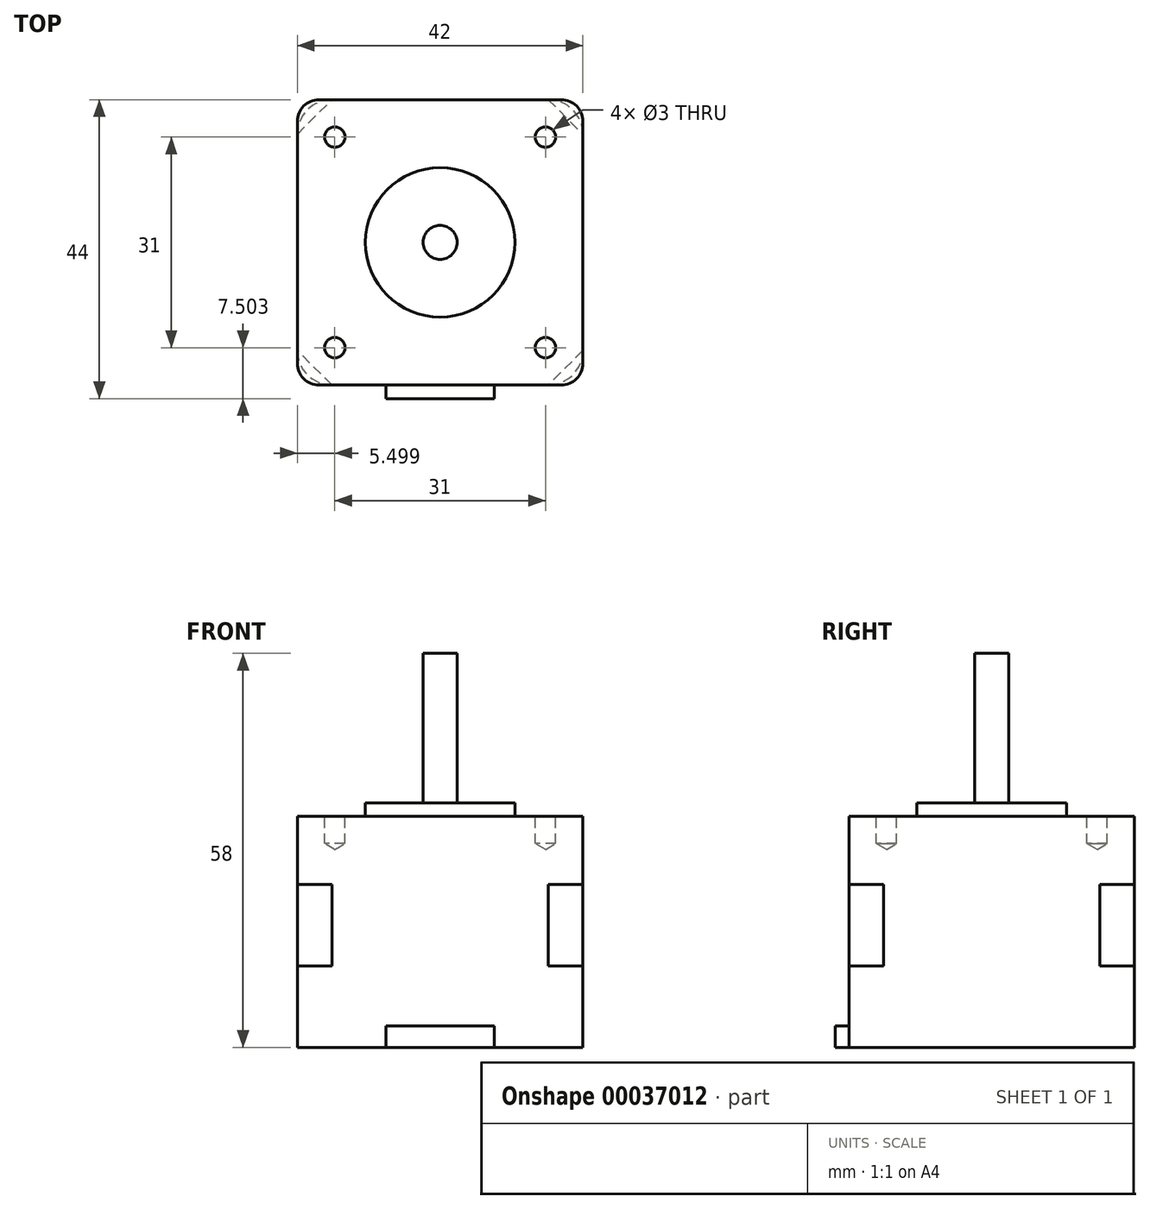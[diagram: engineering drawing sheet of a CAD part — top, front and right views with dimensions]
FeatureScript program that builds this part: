
annotation { "Feature Type Name" : "Feature", "Feature Type Description" : "" }
export const myFeature = defineFeature(function(context is Context, id is Id, definition is map)
    precondition{}
    {
        {
            var Q0;
            Q0=qCreatedBy(makeId("Top.planeOp"),FACE);
            var sketch = newSketch(context, id + "F0", { "sketchPlane" : qUnion([Q0])});
            skLineSegment(sketch, "E0.bottom", {"start": v(-20.04, 16.68) * mm, "end": v(21.96, 16.68) * mm});
            skLineSegment(sketch, "E0.top", {"start": v(-20.04, -25.32) * mm, "end": v(21.96, -25.32) * mm});
            skLineSegment(sketch, "E0.left", {"start": v(-20.04, 16.68) * mm, "end": v(-20.04, -25.32) * mm});
            skLineSegment(sketch, "E0.right", {"start": v(21.96, 16.68) * mm, "end": v(21.96, -25.32) * mm});
            skSolve(sketch);
        }
        {
            var Q0;
            Q0=makeQuery(id+"F0.imprint","IMPRINT",FACE,{"disambiguationData":[TD([[makeQuery(id+"F0.imprint","IMPRINT",EDGE,{"derivedFrom":sQuery(id+"F0.wireOp",EDGE,"E0.bottom")}),-1.0]])]});
            extrude(context, id + "F1", {"entities" : qUnion([Q0]), "depth" : 10 * mm});
        }
        {
            var Q0;
            Q0=makeQuery(id+"F1.opExtrude","CAP_FACE",FACE,{"disambiguationData":[OSD([sQuery(id+"F0.wireOp",EDGE,"E0.bottom"),sQuery(id+"F0.wireOp",EDGE,"E0.top"),sQuery(id+"F0.wireOp",EDGE,"E0.left"),sQuery(id+"F0.wireOp",EDGE,"E0.right")])],"isStart":false});
            var sketch = newSketch(context, id + "F2", { "sketchPlane" : qUnion([Q0])});
            skLineSegment(sketch, "E1", {"start": v(-20.04, 16.68) * mm, "end": v(21.96, -25.32) * mm, "construction": true});
            skLineSegment(sketch, "E2", {"start": v(21.96, 16.68) * mm, "end": v(-20.04, -25.32) * mm, "construction": true});
            skCircle(sketch, "E3", {"center": v(0.96, -4.32) * mm, "radius": 11 * mm});
            skSolve(sketch);
        }
        {
            var Q0;
            Q0=makeQuery(id+"F2.imprint","IMPRINT",FACE,{"disambiguationData":[TD([[makeQuery(id+"F2.imprint","IMPRINT",EDGE,{"derivedFrom":sQuery(id+"F2.wireOp",EDGE,"E3")}),1.0]])]});
            extrude(context, id + "F3", {"entities" : qUnion([Q0]), "operationType" : NewBodyOperationType.ADD, "depth" : 2 * mm});
        }
        {
            var Q0;
            Q0=makeQuery(id+"F1.opExtrude","SWEPT_EDGE",EDGE,{"disambiguationData":[OSD([sQuery(id+"F0.wireOp",EDGE,"E0.top"),sQuery(id+"F0.wireOp",EDGE,"E0.right")])]});
            var Q1;
            Q1=makeQuery(id+"F1.opExtrude","SWEPT_EDGE",EDGE,{"disambiguationData":[OSD([sQuery(id+"F0.wireOp",EDGE,"E0.bottom"),sQuery(id+"F0.wireOp",EDGE,"E0.right")])]});
            var Q2;
            Q2=makeQuery(id+"F1.opExtrude","SWEPT_EDGE",EDGE,{"disambiguationData":[OSD([sQuery(id+"F0.wireOp",EDGE,"E0.bottom"),sQuery(id+"F0.wireOp",EDGE,"E0.left")])]});
            var Q3;
            Q3=makeQuery(id+"F1.opExtrude","SWEPT_EDGE",EDGE,{"disambiguationData":[OSD([sQuery(id+"F0.wireOp",EDGE,"E0.top"),sQuery(id+"F0.wireOp",EDGE,"E0.left")])]});
            fillet(context, id + "F4", {"entities" : qUnion([Q0, Q1, Q2, Q3]), "radius" : 3.17 * mm, "tangentPropagation" : true, "allowEdgeOverflow" : false});
        }
        {
            var Q0;
            Q0=makeQuery(id+"F1.opExtrude","CAP_FACE",FACE,{"disambiguationData":[OSD([sQuery(id+"F0.wireOp",EDGE,"E0.bottom"),sQuery(id+"F0.wireOp",EDGE,"E0.top"),sQuery(id+"F0.wireOp",EDGE,"E0.left"),sQuery(id+"F0.wireOp",EDGE,"E0.right")])],"isStart":true});
            var sketch = newSketch(context, id + "F5", { "sketchPlane" : qUnion([Q0])});
            skLineSegment(sketch, "E4", {"start": v(-20.04, -11.6) * mm, "end": v(-20.04, 20.24) * mm});
            skLineSegment(sketch, "E5", {"start": v(0.96, 25.32) * mm, "end": v(0.96, -16.68) * mm, "construction": true});
            skLineSegment(sketch, "E6", {"start": v(-14.96, 25.32) * mm, "end": v(0.96, 25.32) * mm});
            skLineSegment(sketch, "E7", {"start": v(-14.96, -16.68) * mm, "end": v(0.96, -16.68) * mm});
            skLineSegment(sketch, "E8.MirrorCS", {"start": v(16.88, 25.32) * mm, "end": v(0.96, 25.32) * mm});
            skLineSegment(sketch, "E9.MirrorCS", {"start": v(21.96, -11.6) * mm, "end": v(21.96, 20.24) * mm});
            skLineSegment(sketch, "E10.MirrorCS", {"start": v(16.88, -16.68) * mm, "end": v(0.96, -16.68) * mm});
            skLineSegment(sketch, "E11.top", {"start": v(-20.04, 20.24) * mm, "end": v(-14.96, 20.24) * mm, "construction": true});
            skLineSegment(sketch, "E11.right", {"start": v(-14.96, 25.32) * mm, "end": v(-14.96, 20.24) * mm, "construction": true});
            skLineSegment(sketch, "E12", {"start": v(-14.96, 25.32) * mm, "end": v(-20.04, 20.24) * mm});
            skPoint(sketch, "E13.orphan", {"position": v(-20.04, 25.32) * mm});
            skLineSegment(sketch, "E14.1.0", {"start": v(-20.04, -11.6) * mm, "end": v(-14.96, -16.68) * mm});
            skLineSegment(sketch, "E14.2.0", {"start": v(16.88, -16.68) * mm, "end": v(21.96, -11.6) * mm});
            skLineSegment(sketch, "E14.3.0", {"start": v(21.96, 20.24) * mm, "end": v(16.88, 25.32) * mm});
            skPoint(sketch, "E14.center", {"position": v(0.96, 4.32) * mm});
            skPoint(sketch, "E15.orphan", {"position": v(21.96, 25.32) * mm});
            skPoint(sketch, "E16.orphan", {"position": v(21.96, -16.68) * mm});
            skPoint(sketch, "E17.orphan", {"position": v(-20.04, -16.68) * mm});
            skSolve(sketch);
        }
        {
            var Q0;
            Q0 = qSketchRegion(id + "F5", true);
            extrude(context, id + "F6", {"entities" : qUnion([Q0]), "operationType" : NewBodyOperationType.ADD, "depth" : 12 * mm});
        }
        {
            var Q0;
            Q0=makeQuery(id+"F6.opExtrude","CAP_FACE",FACE,{"disambiguationData":[OSD([sQuery(id+"F5.wireOp",EDGE,"E4"),sQuery(id+"F5.wireOp",EDGE,"E6"),sQuery(id+"F5.wireOp",EDGE,"E7"),sQuery(id+"F5.wireOp",EDGE,"E8.MirrorCS"),sQuery(id+"F5.wireOp",EDGE,"E9.MirrorCS"),sQuery(id+"F5.wireOp",EDGE,"E10.MirrorCS"),sQuery(id+"F5.wireOp",EDGE,"E12"),sQuery(id+"F5.wireOp",EDGE,"E14.1.0"),sQuery(id+"F5.wireOp",EDGE,"E14.2.0"),sQuery(id+"F5.wireOp",EDGE,"E14.3.0")])],"isStart":false});
            var sketch = newSketch(context, id + "F7", { "sketchPlane" : qUnion([Q0])});
            skLineSegment(sketch, "E18.bottom", {"start": v(-20.04, 25.32) * mm, "end": v(21.96, 25.32) * mm});
            skLineSegment(sketch, "E18.top", {"start": v(-20.04, -16.68) * mm, "end": v(21.96, -16.68) * mm});
            skLineSegment(sketch, "E18.left", {"start": v(-20.04, 25.32) * mm, "end": v(-20.04, -16.68) * mm});
            skLineSegment(sketch, "E18.right", {"start": v(21.96, 25.32) * mm, "end": v(21.96, -16.68) * mm});
            skSolve(sketch);
        }
        {
            var Q0;
            Q0 = qSketchRegion(id + "F7", true);
            extrude(context, id + "F8", {"entities" : qUnion([Q0]), "operationType" : NewBodyOperationType.ADD, "depth" : 12 * mm});
        }
        {
            var Q0;
            Q0=makeQuery(id+"F8.opExtrude","SWEPT_EDGE",EDGE,{"disambiguationData":[OSD([sQuery(id+"F7.wireOp",EDGE,"E18.top"),sQuery(id+"F7.wireOp",EDGE,"E18.right")])]});
            var Q1;
            Q1=makeQuery(id+"F8.opExtrude","SWEPT_EDGE",EDGE,{"disambiguationData":[OSD([sQuery(id+"F7.wireOp",EDGE,"E18.bottom"),sQuery(id+"F7.wireOp",EDGE,"E18.right")])]});
            var Q2;
            Q2=makeQuery(id+"F8.opExtrude","SWEPT_EDGE",EDGE,{"disambiguationData":[OSD([sQuery(id+"F7.wireOp",EDGE,"E18.top"),sQuery(id+"F7.wireOp",EDGE,"E18.left")])]});
            var Q3;
            Q3=makeQuery(id+"F8.opExtrude","SWEPT_EDGE",EDGE,{"disambiguationData":[OSD([sQuery(id+"F7.wireOp",EDGE,"E18.bottom"),sQuery(id+"F7.wireOp",EDGE,"E18.left")])]});
            fillet(context, id + "F9", {"entities" : qUnion([Q0, Q1, Q2, Q3]), "radius" : 5.08 * mm, "tangentPropagation" : true, "allowEdgeOverflow" : false});
        }
        {
            var Q0;
            Q0=makeQuery(id+"F1.opExtrude","CAP_FACE",FACE,{"disambiguationData":[OSD([sQuery(id+"F0.wireOp",EDGE,"E0.bottom"),sQuery(id+"F0.wireOp",EDGE,"E0.top"),sQuery(id+"F0.wireOp",EDGE,"E0.left"),sQuery(id+"F0.wireOp",EDGE,"E0.right")])],"isStart":false});
            var sketch = newSketch(context, id + "F10", { "sketchPlane" : qUnion([Q0])});
            skLineSegment(sketch, "E19.bottom", {"start": v(0.96, -4.32) * mm, "end": v(-14.54, -4.32) * mm, "construction": true});
            skLineSegment(sketch, "E19.top", {"start": v(0.96, 11.18) * mm, "end": v(-14.54, 11.18) * mm, "construction": true});
            skLineSegment(sketch, "E19.left", {"start": v(0.96, -4.32) * mm, "end": v(0.96, 11.18) * mm, "construction": true});
            skLineSegment(sketch, "E19.right", {"start": v(-14.54, -4.32) * mm, "end": v(-14.54, 11.18) * mm, "construction": true});
            skCircle(sketch, "E20", {"center": v(-14.54, 11.18) * mm, "radius": 1.5 * mm});
            skCircle(sketch, "E21.0.1.0", {"center": v(-14.54, -19.82) * mm, "radius": 1.5 * mm});
            skCircle(sketch, "E21.1.0.0", {"center": v(16.46, 11.18) * mm, "radius": 1.5 * mm});
            skCircle(sketch, "E21.1.1.0", {"center": v(16.46, -19.82) * mm, "radius": 1.5 * mm});
            skLineSegment(sketch, "E21.direction1", {"start": v(-14.54, 11.18) * mm, "end": v(16.46, 11.18) * mm, "construction": true});
            skLineSegment(sketch, "E21.direction2", {"start": v(-14.54, 11.18) * mm, "end": v(-14.54, -19.82) * mm, "construction": true});
            skSolve(sketch);
        }
        {
            var Q0;
            Q0=sQuery(id+"F10.wireOp",VERTEX,"E20.center");
            var Q1;
            Q1=sQuery(id+"F10.wireOp",VERTEX,"E21.direction2.end");
            var Q2;
            Q2=sQuery(id+"F10.wireOp",VERTEX,"E21.1.1.0.center");
            var Q3;
            Q3=sQuery(id+"F10.wireOp",VERTEX,"E21.direction1.end");
            var Q4;
            Q4=makeQuery(id+"F1.opExtrude","SWEPT_BODY",BODY,{"disambiguationData":[OSD([sQuery(id+"F0.wireOp",EDGE,"E0.bottom"),sQuery(id+"F0.wireOp",EDGE,"E0.top"),sQuery(id+"F0.wireOp",EDGE,"E0.left"),sQuery(id+"F0.wireOp",EDGE,"E0.right")])]});
            hole(context, id + "F11", {"style" : HoleStyle.SIMPLE, "holeDiameter" : 3 * mm, "endStyle" : HoleEndStyle.BLIND, "holeDepth" : 4 * mm, "locations" : qUnion([Q0, Q1, Q2, Q3]), "scope" : qUnion([Q4])});
        }
        {
            var Q0;
            Q0=makeQuery(id+"F3.opExtrude","CAP_FACE",FACE,{"disambiguationData":[OSD([sQuery(id+"F2.wireOp",EDGE,"E3")])],"isStart":false});
            var sketch = newSketch(context, id + "F12", { "sketchPlane" : qUnion([Q0])});
            skCircle(sketch, "E22", {"center": v(0.96, -4.32) * mm, "radius": 2.5 * mm});
            skSolve(sketch);
        }
        {
            var Q0;
            Q0 = qSketchRegion(id + "F12", true);
            extrude(context, id + "F13", {"entities" : qUnion([Q0]), "operationType" : NewBodyOperationType.ADD, "depth" : 22 * mm});
        }
        {
            var Q0;
            Q0=makeQuery(id+"F8.boolean.opBoolean","MERGE",FACE,{"derivedFrom":[makeQuery(id+"F6.boolean.opBoolean","MERGE",FACE,{"derivedFrom":[makeQuery(id+"F1.opExtrude","SWEPT_FACE",FACE,{"disambiguationData":[OSD([sQuery(id+"F0.wireOp",EDGE,"E0.top")])]}),makeQuery(id+"F6.opExtrude","SWEPT_FACE",FACE,{"disambiguationData":[OSD([sQuery(id+"F5.wireOp",EDGE,"E6"),sQuery(id+"F5.wireOp",EDGE,"E8.MirrorCS")])]})]}),makeQuery(id+"F8.opExtrude","SWEPT_FACE",FACE,{"disambiguationData":[OSD([sQuery(id+"F7.wireOp",EDGE,"E18.bottom")])]})]});
            var sketch = newSketch(context, id + "F14", { "sketchPlane" : qUnion([Q0])});
            skLineSegment(sketch, "E23.bottom", {"start": v(0.96, -24) * mm, "end": v(8.9, -24) * mm});
            skLineSegment(sketch, "E23.top", {"start": v(0.96, -20.88) * mm, "end": v(8.9, -20.88) * mm});
            skLineSegment(sketch, "E23.left", {"start": v(0.96, -24) * mm, "end": v(0.96, -20.88) * mm, "construction": true});
            skLineSegment(sketch, "E23.right", {"start": v(8.9, -24) * mm, "end": v(8.9, -20.88) * mm});
            skLineSegment(sketch, "E24.MirrorCS", {"start": v(0.96, -20.88) * mm, "end": v(-6.99, -20.88) * mm});
            skLineSegment(sketch, "E25.MirrorCS", {"start": v(-6.99, -24) * mm, "end": v(-6.99, -20.88) * mm});
            skLineSegment(sketch, "E26.MirrorCS", {"start": v(0.96, -24) * mm, "end": v(-6.99, -24) * mm});
            skSolve(sketch);
        }
        {
            var Q0;
            Q0=makeQuery(id+"F14.imprint","IMPRINT",FACE,{"disambiguationData":[TD([[makeQuery(id+"F14.imprint","IMPRINT",EDGE,{"derivedFrom":sQuery(id+"F14.wireOp",EDGE,"E23.bottom")}),1.0]])]});
            var Q1;
            Q1=sQuery(id+"F14.wireOp",EDGE,"E23.bottom");
            var Q2;
            Q2=sQuery(id+"F14.wireOp",EDGE,"E26.MirrorCS");
            var Q3;
            Q3=sQuery(id+"F14.wireOp",EDGE,"E25.MirrorCS");
            var Q4;
            Q4=sQuery(id+"F14.wireOp",EDGE,"E24.MirrorCS");
            var Q5;
            Q5=sQuery(id+"F14.wireOp",EDGE,"E23.top");
            var Q6;
            Q6=sQuery(id+"F14.wireOp",EDGE,"E23.right");
            extrude(context, id + "F15", {"entities" : qUnion([Q0]), "operationType" : NewBodyOperationType.ADD, "surfaceEntities" : qUnion([Q1, Q2, Q3, Q4, Q5, Q6]), "depth" : 2 * mm});
        }
    });
